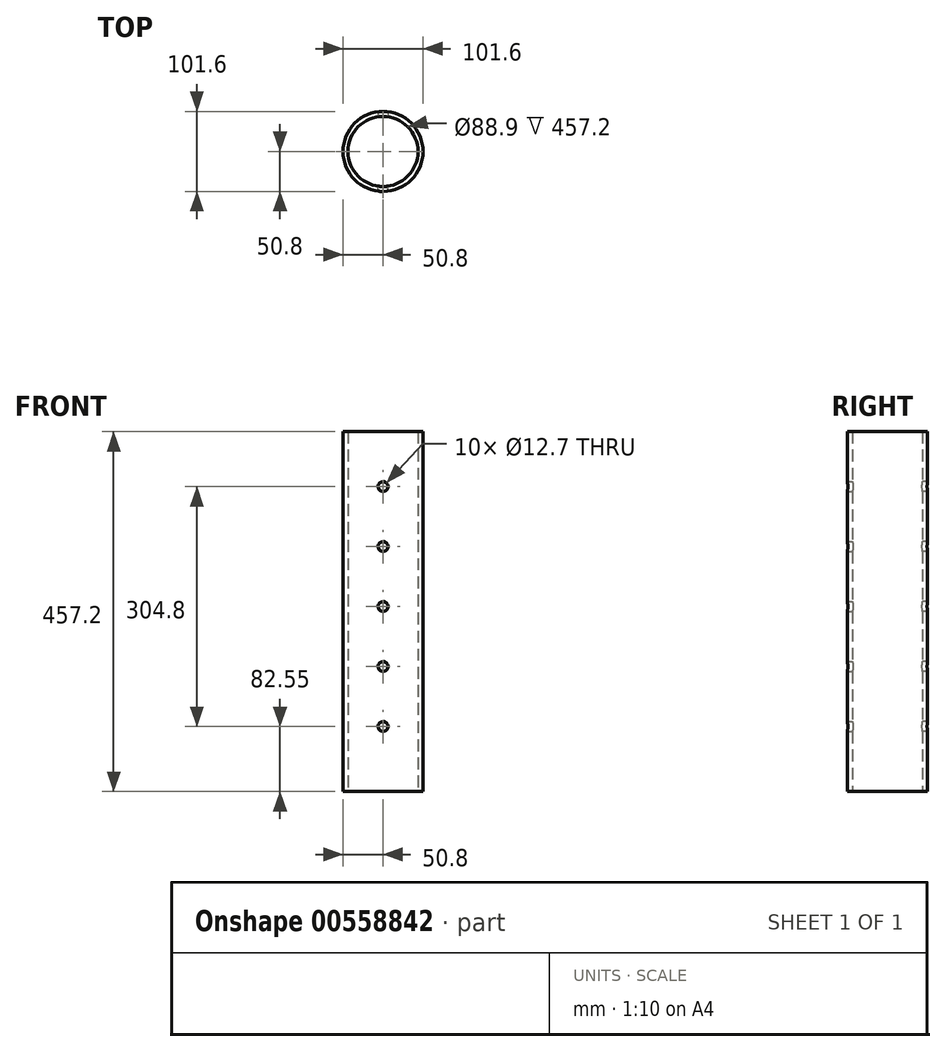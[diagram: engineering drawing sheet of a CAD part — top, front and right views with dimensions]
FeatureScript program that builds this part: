
annotation { "Feature Type Name" : "Feature", "Feature Type Description" : "" }
export const myFeature = defineFeature(function(context is Context, id is Id, definition is map)
    precondition{}
    {
        {
            var Q0;
            Q0=qCreatedBy(makeId("Top.planeOp"),FACE);
            var sketch = newSketch(context, id + "F0", { "sketchPlane" : qUnion([Q0])});
            skCircle(sketch, "E0", {"center": v(0, 0) * mm, "radius": 50.8 * mm});
            skCircle(sketch, "E1", {"center": v(0, 0) * mm, "radius": 44.45 * mm});
            skSolve(sketch);
        }
        {
            var Q0;
            Q0=qCreatedBy(makeId("Front.planeOp"),FACE);
            var sketch = newSketch(context, id + "F1", { "sketchPlane" : qUnion([Q0])});
            skCircle(sketch, "E2", {"center": v(0, 82.55) * mm, "radius": 6.35 * mm});
            skCircle(sketch, "E3.0.1.0", {"center": v(0, 158.75) * mm, "radius": 6.35 * mm});
            skCircle(sketch, "E3.0.2.0", {"center": v(0, 234.95) * mm, "radius": 6.35 * mm});
            skCircle(sketch, "E3.0.3.0", {"center": v(0, 311.15) * mm, "radius": 6.35 * mm});
            skCircle(sketch, "E3.0.4.0", {"center": v(0, 387.35) * mm, "radius": 6.35 * mm});
            skLineSegment(sketch, "E3.direction1", {"start": v(0, 82.55) * mm, "end": v(25.4, 82.55) * mm, "construction": true});
            skLineSegment(sketch, "E3.direction2", {"start": v(0, 82.55) * mm, "end": v(0, 158.75) * mm, "construction": true});
            skSolve(sketch);
        }
        {
            var Q0;
            Q0 = qSketchRegion(id + "F0", true);
            extrude(context, id + "F2", {"entities" : qUnion([Q0]), "depth" : 457.2 * mm, "offsetDistance" : 25.4 * mm});
        }
        {
            var Q0;
            Q0 = qSketchRegion(id + "F1", true);
            extrude(context, id + "F3", {"entities" : qUnion([Q0]), "operationType" : NewBodyOperationType.REMOVE, "endBound" : BoundingType.THROUGH_ALL, "depth" : 25.4 * mm, "offsetDistance" : 25.4 * mm});
        }
        {
            var Q0;
            Q0 = qSketchRegion(id + "F1", true);
            extrude(context, id + "F4", {"entities" : qUnion([Q0]), "operationType" : NewBodyOperationType.REMOVE, "endBound" : BoundingType.THROUGH_ALL, "oppositeDirection" : true, "depth" : 25.4 * mm, "offsetDistance" : 25.4 * mm});
        }
    });
